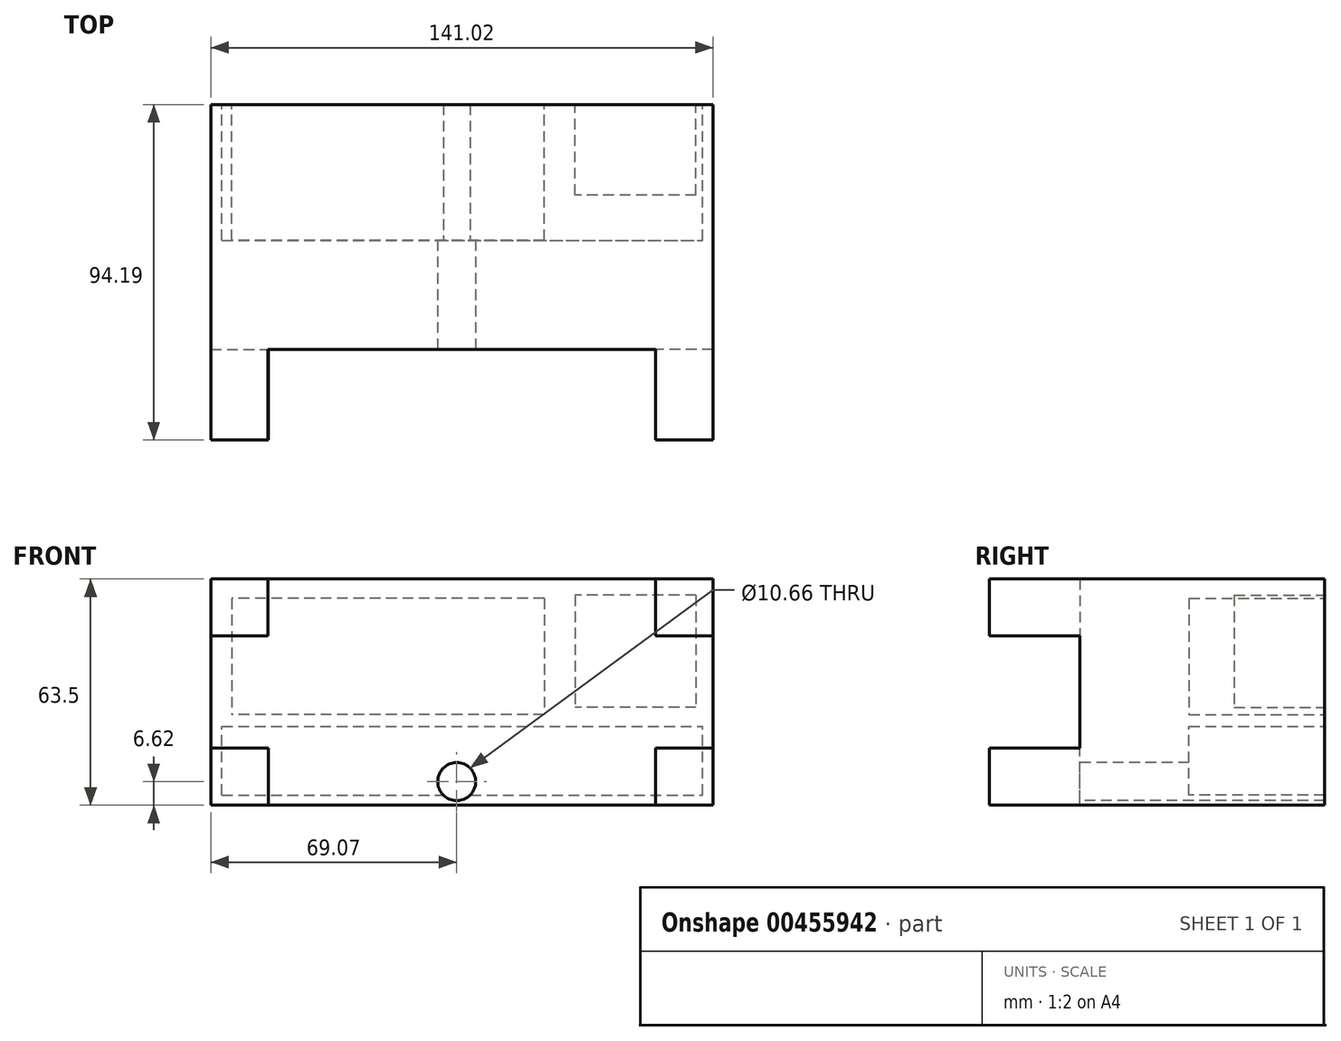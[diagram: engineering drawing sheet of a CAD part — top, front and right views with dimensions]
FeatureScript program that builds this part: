
annotation { "Feature Type Name" : "Feature", "Feature Type Description" : "" }
export const myFeature = defineFeature(function(context is Context, id is Id, definition is map)
    precondition{}
    {
        {
            var Q0;
            Q0=qCreatedBy(makeId("Top.planeOp"),FACE);
            var sketch = newSketch(context, id + "F0", { "sketchPlane" : qUnion([Q0])});
            skLineSegment(sketch, "E0.bottom", {"start": v(-53.82, 3.17) * mm, "end": v(53.82, 3.17) * mm});
            skLineSegment(sketch, "E0.top", {"start": v(-53.82, -3.17) * mm, "end": v(53.82, -3.17) * mm});
            skLineSegment(sketch, "E0.left", {"start": v(-53.82, 3.17) * mm, "end": v(-53.82, -3.17) * mm});
            skLineSegment(sketch, "E0.right", {"start": v(53.82, 3.17) * mm, "end": v(53.82, -3.17) * mm});
            skPoint(sketch, "E0.middle", {"position": v(0, 0) * mm});
            skSolve(sketch);
        }
        {
            var Q0;
            Q0 = qSketchRegion(id + "F0", true);
            extrude(context, id + "F1", {"entities" : qUnion([Q0]), "depth" : mm});
        }
        {
            var Q0;
            Q0=makeQuery(id+"F1.opExtrude","SWEPT_BODY",BODY,{"disambiguationData":[OSD([sQuery(id+"F0.wireOp",EDGE,"E0.bottom"),sQuery(id+"F0.wireOp",EDGE,"E0.top"),sQuery(id+"F0.wireOp",EDGE,"E0.left"),sQuery(id+"F0.wireOp",EDGE,"E0.right")])]});
            deleteBodies(context, id + "F2", {"entities" : qUnion([Q0])});
        }
        {
            var Q0;
            Q0=qCreatedBy(makeId("Top.planeOp"),FACE);
            var sketch = newSketch(context, id + "F3", { "sketchPlane" : qUnion([Q0])});
            skLineSegment(sketch, "E1.bottom", {"start": v(-69.07, 30.5) * mm, "end": v(71.95, 30.5) * mm});
            skLineSegment(sketch, "E1.top", {"start": v(-69.07, -38.28) * mm, "end": v(71.95, -38.28) * mm});
            skLineSegment(sketch, "E1.left", {"start": v(-69.07, 30.5) * mm, "end": v(-69.07, -38.28) * mm});
            skLineSegment(sketch, "E1.right", {"start": v(71.95, 30.5) * mm, "end": v(71.95, -38.28) * mm});
            skSolve(sketch);
        }
        {
            var Q0;
            Q0=makeQuery(id+"F3.imprint","IMPRINT",FACE,{"disambiguationData":[TD([[makeQuery(id+"F3.imprint","IMPRINT",EDGE,{"derivedFrom":sQuery(id+"F3.wireOp",EDGE,"E1.bottom")}),-1.0]])]});
            extrude(context, id + "F4", {"entities" : qUnion([Q0]), "depth" : 63.5 * mm});
        }
        {
            var Q0;
            Q0=makeQuery(id+"F4.opExtrude","SWEPT_FACE",FACE,{"disambiguationData":[OSD([sQuery(id+"F3.wireOp",EDGE,"E1.bottom")])]});
            var sketch = newSketch(context, id + "F5", { "sketchPlane" : qUnion([Q0])});
            skLineSegment(sketch, "E2.bottom", {"start": v(65.9, 2.88) * mm, "end": v(-69.07, 2.88) * mm});
            skLineSegment(sketch, "E2.top", {"start": v(65.9, 22.16) * mm, "end": v(-69.07, 22.16) * mm});
            skLineSegment(sketch, "E2.left", {"start": v(65.9, 2.88) * mm, "end": v(65.9, 22.16) * mm});
            skLineSegment(sketch, "E2.right", {"start": v(-69.07, 2.88) * mm, "end": v(-69.07, 22.16) * mm});
            skSolve(sketch);
        }
        {
            var Q0;
            Q0 = qSketchRegion(id + "F5", true);
            extrude(context, id + "F6", {"entities" : qUnion([Q0]), "operationType" : NewBodyOperationType.REMOVE, "oppositeDirection" : true, "depth" : 38.1 * mm});
        }
        {
            var Q0;
            Q0=makeQuery(id+"F4.opExtrude","SWEPT_FACE",FACE,{"disambiguationData":[OSD([sQuery(id+"F3.wireOp",EDGE,"E1.bottom")])]});
            var sketch = newSketch(context, id + "F7", { "sketchPlane" : qUnion([Q0])});
            skLineSegment(sketch, "E3.bottom", {"start": v(-67.16, 58.96) * mm, "end": v(-33.2, 58.96) * mm});
            skLineSegment(sketch, "E3.top", {"start": v(-67.16, 27.53) * mm, "end": v(-33.2, 27.53) * mm});
            skLineSegment(sketch, "E3.left", {"start": v(-67.16, 58.96) * mm, "end": v(-67.16, 27.53) * mm});
            skLineSegment(sketch, "E3.right", {"start": v(-33.2, 58.96) * mm, "end": v(-33.2, 27.53) * mm});
            skSolve(sketch);
        }
        {
            var Q0;
            Q0 = qSketchRegion(id + "F7", true);
            extrude(context, id + "F8", {"entities" : qUnion([Q0]), "operationType" : NewBodyOperationType.REMOVE, "oppositeDirection" : true, "depth" : 25.4 * mm});
        }
        {
            var Q0;
            Q0=makeQuery(id+"F4.opExtrude","SWEPT_FACE",FACE,{"disambiguationData":[OSD([sQuery(id+"F3.wireOp",EDGE,"E1.bottom")])]});
            var sketch = newSketch(context, id + "F9", { "sketchPlane" : qUnion([Q0])});
            skLineSegment(sketch, "E4.bottom", {"start": v(-24.6, 58.04) * mm, "end": v(63.12, 58.04) * mm});
            skLineSegment(sketch, "E4.top", {"start": v(-24.6, 25.45) * mm, "end": v(63.12, 25.45) * mm});
            skLineSegment(sketch, "E4.left", {"start": v(-24.6, 58.04) * mm, "end": v(-24.6, 25.45) * mm});
            skLineSegment(sketch, "E4.right", {"start": v(63.12, 58.04) * mm, "end": v(63.12, 25.45) * mm});
            skSolve(sketch);
        }
        {
            var Q0;
            Q0 = qSketchRegion(id + "F9", true);
            extrude(context, id + "F10", {"entities" : qUnion([Q0]), "operationType" : NewBodyOperationType.REMOVE, "oppositeDirection" : true, "depth" : 38.1 * mm});
        }
        {
            var Q0;
            Q0=makeQuery(id+"F4.opExtrude","SWEPT_FACE",FACE,{"disambiguationData":[OSD([sQuery(id+"F3.wireOp",EDGE,"E1.top")])]});
            var sketch = newSketch(context, id + "F11", { "sketchPlane" : qUnion([Q0])});
            skLineSegment(sketch, "E5.bottom", {"start": v(-69.07, 63.5) * mm, "end": v(-52.96, 63.5) * mm});
            skLineSegment(sketch, "E5.top", {"start": v(-69.07, 47.49) * mm, "end": v(-52.96, 47.49) * mm});
            skLineSegment(sketch, "E5.left", {"start": v(-69.07, 63.5) * mm, "end": v(-69.07, 47.49) * mm});
            skLineSegment(sketch, "E5.right", {"start": v(-52.96, 63.5) * mm, "end": v(-52.96, 47.49) * mm});
            skLineSegment(sketch, "E6.bottom", {"start": v(71.95, 63.5) * mm, "end": v(55.83, 63.5) * mm});
            skLineSegment(sketch, "E6.top", {"start": v(71.95, 47.49) * mm, "end": v(55.83, 47.49) * mm});
            skLineSegment(sketch, "E6.left", {"start": v(71.95, 63.5) * mm, "end": v(71.95, 47.49) * mm});
            skLineSegment(sketch, "E6.right", {"start": v(55.83, 63.5) * mm, "end": v(55.83, 47.49) * mm});
            skLineSegment(sketch, "E7.bottom", {"start": v(-69.07, 0) * mm, "end": v(-52.94, 0) * mm});
            skLineSegment(sketch, "E7.top", {"start": v(-69.07, 16) * mm, "end": v(-52.94, 16) * mm});
            skLineSegment(sketch, "E7.left", {"start": v(-69.07, 0) * mm, "end": v(-69.07, 16) * mm});
            skLineSegment(sketch, "E7.right", {"start": v(-52.94, 0) * mm, "end": v(-52.94, 16) * mm});
            skLineSegment(sketch, "E8.bottom", {"start": v(71.95, 0) * mm, "end": v(55.82, 0) * mm});
            skLineSegment(sketch, "E8.top", {"start": v(71.95, 16) * mm, "end": v(55.82, 16) * mm});
            skLineSegment(sketch, "E8.left", {"start": v(71.95, 0) * mm, "end": v(71.95, 16) * mm});
            skLineSegment(sketch, "E8.right", {"start": v(55.82, 0) * mm, "end": v(55.82, 16) * mm});
            skSolve(sketch);
        }
        {
            var Q0;
            Q0 = qSketchRegion(id + "F11", true);
            extrude(context, id + "F12", {"entities" : qUnion([Q0]), "operationType" : NewBodyOperationType.ADD, "depth" : 25.4 * mm});
        }
        {
            var Q0;
            Q0=makeQuery(id+"F4.opExtrude","SWEPT_FACE",FACE,{"disambiguationData":[OSD([sQuery(id+"F3.wireOp",EDGE,"E1.top")])]});
            var sketch = newSketch(context, id + "F13", { "sketchPlane" : qUnion([Q0])});
            skCircle(sketch, "E9", {"center": v(0, 6.62) * mm, "radius": 5.33 * mm});
            skSolve(sketch);
        }
        {
            var Q0;
            Q0 = qSketchRegion(id + "F13", true);
            extrude(context, id + "F14", {"entities" : qUnion([Q0]), "operationType" : NewBodyOperationType.REMOVE, "oppositeDirection" : true, "depth" : 101.6 * mm});
        }
    });
